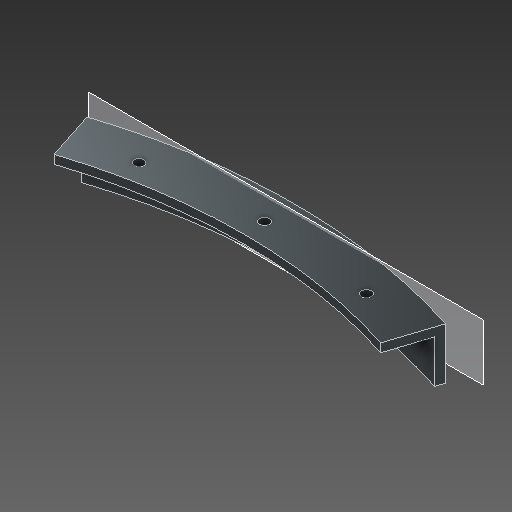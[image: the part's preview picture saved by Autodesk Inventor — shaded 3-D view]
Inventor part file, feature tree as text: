
AUTODESK INVENTOR PART (.ipt)
format: ipt  version: 2020 (Build 240168000, 168)  size: 167,424 bytes
history: native  units: in
note: dims shown in document units (in); Inventor stores cm internally (conversion verified against a paired STEP export)
features: extrude x4, sketch x4, plane x1
ambient origin geometry x8: Origin, YZ Plane, XZ Plane, XY Plane, X Axis, Y Axis, Z Axis, Center Point
bodies: Solid1 (feature_tree)
feature tree (9):
  extrude  "Extrusion1"  Depth=0.7421in
  extrude  "Extrusion2"  Depth=0.1181in
  extrude  "Extrusion3"  Depth=0.1181in
  plane  "Work Plane1"
  extrude  "Extrusion4"  Depth=0.3937in
  sketch  "Sketch1"  dims[d0=15.748in d1=0.7421in]
  sketch  "Sketch3"  dims[d2=0.4947in d4=0.1181in]
  sketch  "Sketch4"  dims[d5=0.1181in d6=0.1181in]
  sketch  "Sketch6"  dims[d7=0.1181in d8=0.5906in d9=0.0in d10=0.0in d12=0.7087in d13=0.7087in d14=0.7087in d15=0.1181in d16=0.0in d17=0.1181in d18=0.2953in d19=0.1378in d20=0.1181in d21=0.0in d22=-7.874in d23=0.1181in d24=0.2953in d25=0.1378in d26=0.3937in d27=0.0in d28=0.1181in d29=0.2953in d30=0.1181in d31=0.2953in d32=1.5748in d33=1.5748in d34=0.1378in d35=0.1378in d36=1.5748in d37=3.1496in d38=0.1378in d39=0.1378in]
